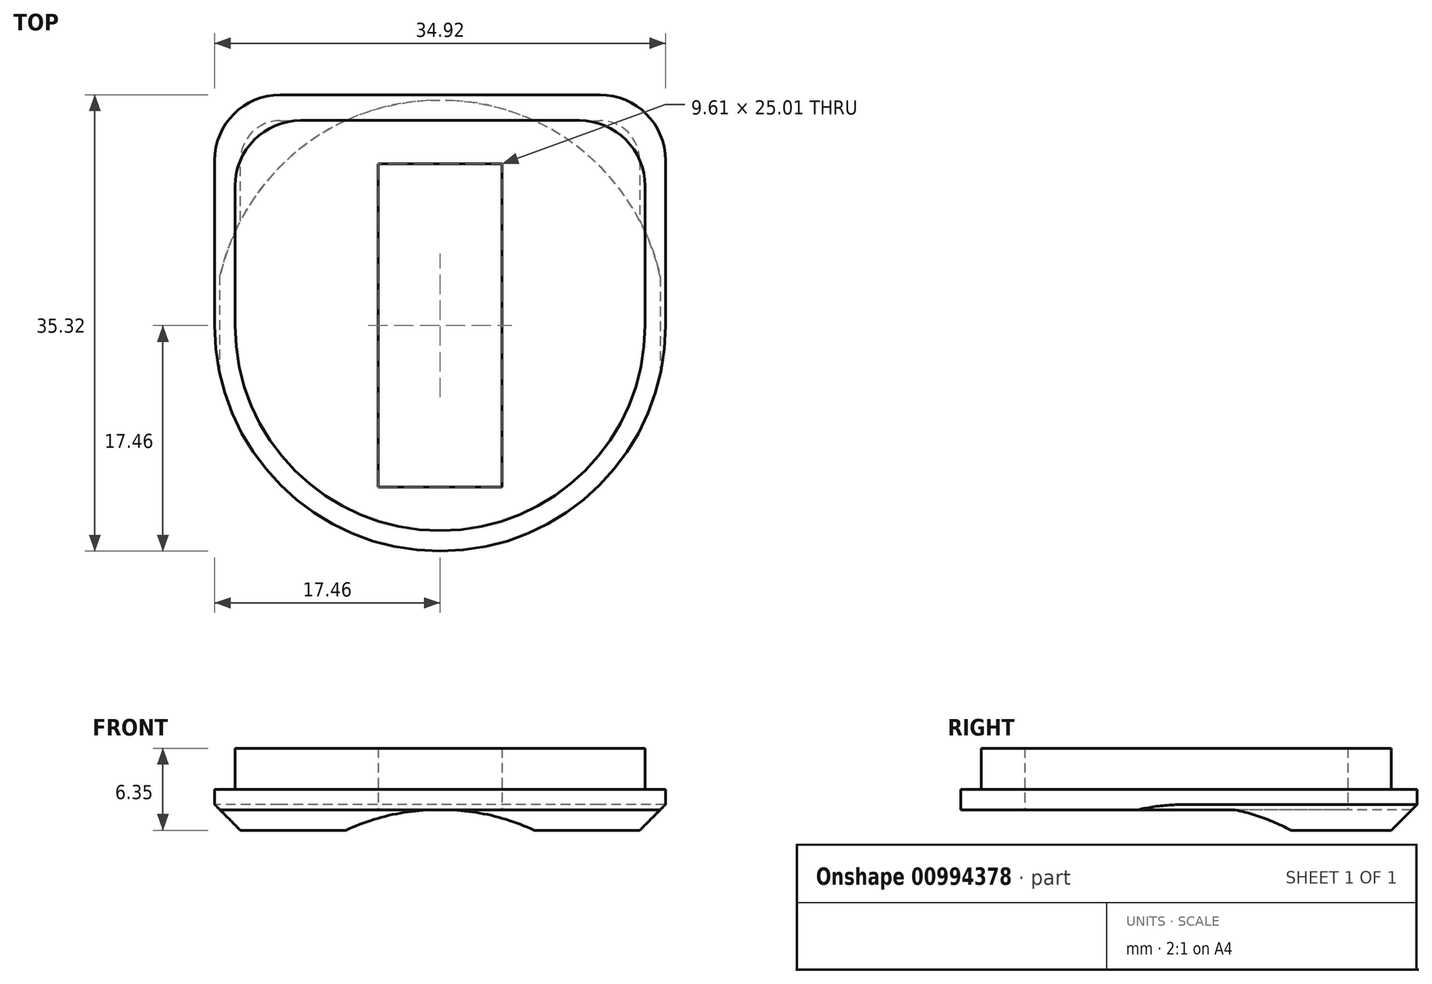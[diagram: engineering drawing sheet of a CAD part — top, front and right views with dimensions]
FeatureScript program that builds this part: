
annotation { "Feature Type Name" : "Feature", "Feature Type Description" : "" }
export const myFeature = defineFeature(function(context is Context, id is Id, definition is map)
    precondition{}
    {
        {
            var Q0;
            Q0=qCreatedBy(makeId("Top.planeOp"),FACE);
            var sketch = newSketch(context, id + "F0", { "sketchPlane" : qUnion([Q0])});
            skCircle(sketch, "E0", {"center": v(0, 0) * mm, "radius": 17.46 * mm});
            skPoint(sketch, "E1", {"position": v(0, 17.46) * mm});
            skPoint(sketch, "E2", {"position": v(17.46, 0) * mm});
            skPoint(sketch, "E3", {"position": v(-17.46, 0) * mm});
            skLineSegment(sketch, "E4", {"start": v(-17.46, 0) * mm, "end": v(-17.46, 17.86) * mm});
            skLineSegment(sketch, "E5", {"start": v(-17.46, 17.86) * mm, "end": v(17.46, 17.86) * mm});
            skLineSegment(sketch, "E6", {"start": v(17.46, 17.86) * mm, "end": v(17.46, 0) * mm});
            skSolve(sketch);
        }
        {
            var Q0;
            Q0 = qSketchRegion(id + "F0", true);
            extrude(context, id + "F1", {"entities" : qUnion([Q0]), "depth" : 3.17 * mm, "offsetDistance" : 25.4 * mm});
        }
        {
            var Q0;
            Q0=makeQuery(id+"F1.opExtrude","CAP_FACE",FACE,{"disambiguationData":[OSD([sQuery(id+"F0.wireOp",EDGE,"E0"),sQuery(id+"F0.wireOp",EDGE,"cv1Jy4IO-z3Q6-1iP2-y0Yy-UG1mujkY5RGA"),sQuery(id+"F0.wireOp",EDGE,"ufQwWpK6-tNk0-q74X-0sZh-Op5Is7e2ByPH"),sQuery(id+"F0.wireOp",EDGE,"IB00LITf-MMwc-QL5Q-mpzT-0WnYT1xAQYxO")])],"isStart":false});
            var sketch = newSketch(context, id + "F2", { "sketchPlane" : qUnion([Q0])});
            skCircle(sketch, "E7", {"center": v(0, 0) * mm, "radius": 15.88 * mm});
            skPoint(sketch, "E8", {"position": v(0, 15.88) * mm});
            skPoint(sketch, "E9", {"position": v(-15.88, 0) * mm});
            skPoint(sketch, "E10", {"position": v(15.88, 0) * mm});
            skLineSegment(sketch, "E11", {"start": v(-15.88, 0) * mm, "end": v(-15.88, 15.88) * mm});
            skLineSegment(sketch, "E12", {"start": v(-15.88, 15.88) * mm, "end": v(15.88, 15.88) * mm});
            skLineSegment(sketch, "E13", {"start": v(15.88, 15.88) * mm, "end": v(15.88, 0) * mm});
            skSolve(sketch);
        }
        {
            var Q0;
            Q0 = qSketchRegion(id + "F2", true);
            extrude(context, id + "F3", {"entities" : qUnion([Q0]), "operationType" : NewBodyOperationType.ADD, "depth" : 3.17 * mm, "offsetDistance" : 25.4 * mm});
        }
        {
            var Q0;
            Q0=makeQuery(id+"F1.opExtrude","CAP_FACE",FACE,{"disambiguationData":[OSD([sQuery(id+"F0.wireOp",EDGE,"E0"),sQuery(id+"F0.wireOp",EDGE,"cv1Jy4IO-z3Q6-1iP2-y0Yy-UG1mujkY5RGA"),sQuery(id+"F0.wireOp",EDGE,"ufQwWpK6-tNk0-q74X-0sZh-Op5Is7e2ByPH"),sQuery(id+"F0.wireOp",EDGE,"IB00LITf-MMwc-QL5Q-mpzT-0WnYT1xAQYxO")])],"isStart":true});
            var sketch = newSketch(context, id + "F4", { "sketchPlane" : qUnion([Q0])});
            skArc(sketch, "E14.0.1", {"start": v(17.46, 0) * mm, "mid": v(0, 17.46) * mm, "end": v(-17.46, 0) * mm});
            skCircle(sketch, "E15", {"center": v(0, 0) * mm, "radius": 17.46 * mm});
            skSolve(sketch);
        }
        {
            var Q0;
            Q0 = qSketchRegion(id + "F4", true);
            extrude(context, id + "F5", {"entities" : qUnion([Q0]), "operationType" : NewBodyOperationType.REMOVE, "oppositeDirection" : true, "depth" : 1.59 * mm, "offsetDistance" : 25.4 * mm});
        }
        {
            var Q0;
            Q0=makeQuery(id+"F5.boolean.opBoolean","COPY",FACE,{"derivedFrom":makeQuery(id+"F5.opExtrude","CAP_FACE",FACE,{"disambiguationData":[OSD([sQuery(id+"F4.wireOp",EDGE,"E15")])],"isStart":false})});
            var sketch = newSketch(context, id + "F6", { "sketchPlane" : qUnion([Q0])});
            skLineSegment(sketch, "E16.bottom", {"start": v(-4.8, -12.5) * mm, "end": v(4.8, -12.5) * mm});
            skLineSegment(sketch, "E16.top", {"start": v(-4.8, 12.5) * mm, "end": v(4.8, 12.5) * mm});
            skLineSegment(sketch, "E16.left", {"start": v(-4.8, -12.5) * mm, "end": v(-4.8, 12.5) * mm});
            skLineSegment(sketch, "E16.right", {"start": v(4.8, -12.5) * mm, "end": v(4.8, 12.5) * mm});
            skPoint(sketch, "E16.middle", {"position": v(0, 0) * mm});
            skSolve(sketch);
        }
        {
            var Q0;
            Q0 = qSketchRegion(id + "F6", true);
            extrude(context, id + "F7", {"entities" : qUnion([Q0]), "operationType" : NewBodyOperationType.REMOVE, "oppositeDirection" : true, "depth" : 25.4 * mm, "offsetDistance" : 25.4 * mm});
        }
        {
            var Q0;
            Q0=makeQuery(id+"F1.opExtrude","SWEPT_EDGE",EDGE,{"disambiguationData":[OSD([sQuery(id+"F0.wireOp",EDGE,"E5"),sQuery(id+"F0.wireOp",EDGE,"E6")])]});
            var Q1;
            Q1=makeQuery(id+"F1.opExtrude","SWEPT_EDGE",EDGE,{"disambiguationData":[OSD([sQuery(id+"F0.wireOp",EDGE,"E4"),sQuery(id+"F0.wireOp",EDGE,"E5")])]});
            var Q2;
            Q2=makeQuery(id+"F3.opExtrude","SWEPT_EDGE",EDGE,{"disambiguationData":[OSD([sQuery(id+"F2.wireOp",EDGE,"E11"),sQuery(id+"F2.wireOp",EDGE,"E12")])]});
            var Q3;
            Q3=makeQuery(id+"F3.opExtrude","SWEPT_EDGE",EDGE,{"disambiguationData":[OSD([sQuery(id+"F2.wireOp",EDGE,"E12"),sQuery(id+"F2.wireOp",EDGE,"E13")])]});
            fillet(context, id + "F8", {"entities" : qUnion([Q0, Q1, Q2, Q3]), "radius" : 5.08 * mm, "tangentPropagation" : true, "allowEdgeOverflow" : false});
        }
        {
            var Q0;
            Q0=makeQuery(id+"F1.opExtrude","CAP_EDGE",EDGE,{"disambiguationData":[OSD([sQuery(id+"F0.wireOp",EDGE,"E6")])],"isStart":true});
            var Q1;
            {var subQ0=sQuery(id+"F0.wireOp",EDGE,"E6");var subQ1=sQuery(id+"F0.wireOp",EDGE,"E5");Q1=makeQuery(id+"F8.opFillet","BLEND_EDGE",EDGE,{"blendedFrom":[makeQuery(id+"F1.opExtrude","SWEPT_EDGE",EDGE,{"disambiguationData":[OSD([subQ1,subQ0])]}),makeQuery(id+"F1.opExtrude","CAP_FACE",FACE,{"disambiguationData":[OSD([sQuery(id+"F0.wireOp",EDGE,"E0"),sQuery(id+"F0.wireOp",EDGE,"E4"),subQ1,subQ0])],"isStart":true})],"blendedInto":[makeQuery(id+"F1.opExtrude","CAP_FACE",FACE,{"disambiguationData":[OSD([sQuery(id+"F0.wireOp",EDGE,"E0"),sQuery(id+"F0.wireOp",EDGE,"E4"),subQ1,subQ0])],"isStart":true})]});}
            chamfer(context, id + "F9", {"entities" : qUnion([Q0, Q1]), "width" : 2 * mm, "tangentPropagation" : true});
        }
    });
